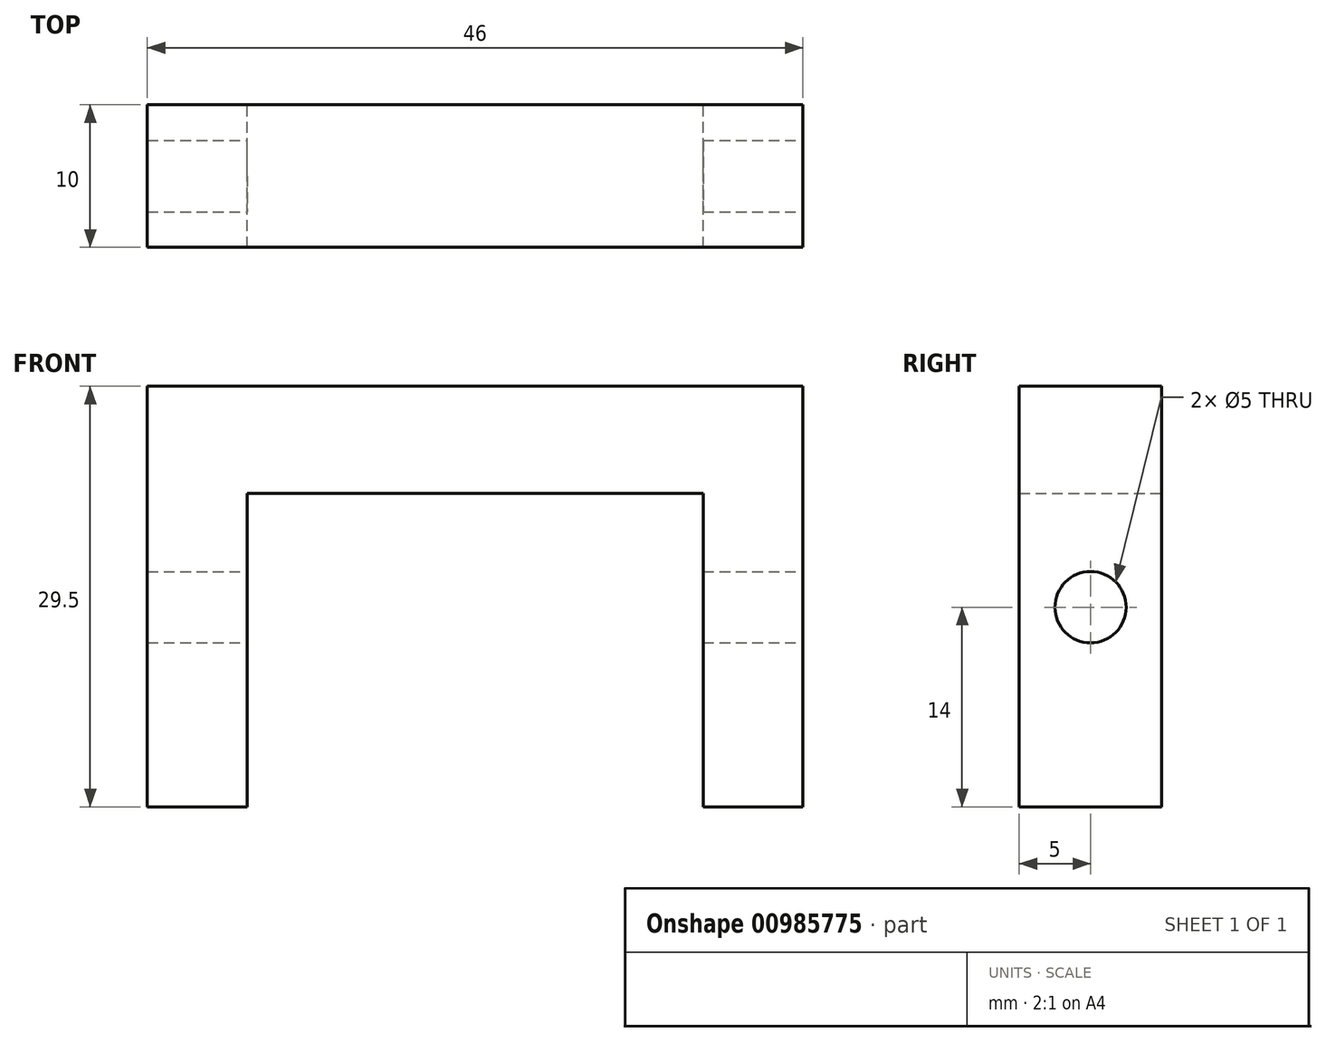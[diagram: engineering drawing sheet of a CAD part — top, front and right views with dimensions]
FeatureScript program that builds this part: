
annotation { "Feature Type Name" : "Feature", "Feature Type Description" : "" }
export const myFeature = defineFeature(function(context is Context, id is Id, definition is map)
    precondition{}
    {
        {
            var Q0;
            Q0=qCreatedBy(makeId("Front.planeOp"),FACE);
            var sketch = newSketch(context, id + "F0", { "sketchPlane" : qUnion([Q0])});
            skLineSegment(sketch, "E0", {"start": v(0, 0) * mm, "end": v(0, 22) * mm});
            skLineSegment(sketch, "E1", {"start": v(0, 22) * mm, "end": v(32, 22) * mm});
            skLineSegment(sketch, "E2", {"start": v(32, 22) * mm, "end": v(32, 0) * mm});
            skLineSegment(sketch, "E3", {"start": v(32, 0) * mm, "end": v(39, 0) * mm});
            skLineSegment(sketch, "E4", {"start": v(39, 0) * mm, "end": v(39, 29.5) * mm});
            skLineSegment(sketch, "E5", {"start": v(39, 29.5) * mm, "end": v(-7, 29.5) * mm});
            skLineSegment(sketch, "E6", {"start": v(-7, 29.5) * mm, "end": v(-7, 0) * mm});
            skLineSegment(sketch, "E7", {"start": v(-7, 0) * mm, "end": v(0, 0) * mm});
            skSolve(sketch);
        }
        {
            var Q0;
            Q0=makeQuery(id+"F0.imprint","IMPRINT",FACE,{"disambiguationData":[TD([[makeQuery(id+"F0.imprint","IMPRINT",EDGE,{"derivedFrom":sQuery(id+"F0.wireOp",EDGE,"E0")}),1.0]])]});
            extrude(context, id + "F1", {"entities" : qUnion([Q0]), "depth" : 10 * mm, "offsetDistance" : 25 * mm});
        }
        {
            var Q0;
            Q0=makeQuery(id+"F1.opExtrude","SWEPT_FACE",FACE,{"disambiguationData":[OSD([sQuery(id+"F0.wireOp",EDGE,"E4")])]});
            var sketch = newSketch(context, id + "F2", { "sketchPlane" : qUnion([Q0])});
            skCircle(sketch, "E8", {"center": v(-5, 14) * mm, "radius": 2.5 * mm});
            skPoint(sketch, "E9", {"position": v(-5, 29.5) * mm});
            skSolve(sketch);
        }
        {
            var Q0;
            Q0=makeQuery(id+"F2.imprint","IMPRINT",FACE,{"disambiguationData":[TD([[makeQuery(id+"F2.imprint","IMPRINT",EDGE,{"derivedFrom":sQuery(id+"F2.wireOp",EDGE,"E8")}),1.0]])]});
            var Q1;
            Q1=makeQuery(id+"F1.opExtrude","SWEPT_FACE",FACE,{"disambiguationData":[OSD([sQuery(id+"F0.wireOp",EDGE,"E6")])]});
            extrude(context, id + "F3", {"entities" : qUnion([Q0]), "operationType" : NewBodyOperationType.REMOVE, "endBound" : BoundingType.UP_TO_SURFACE, "oppositeDirection" : true, "depth" : 25 * mm, "endBoundEntityFace" : qUnion([Q1]), "offsetDistance" : 25 * mm});
        }
    });
